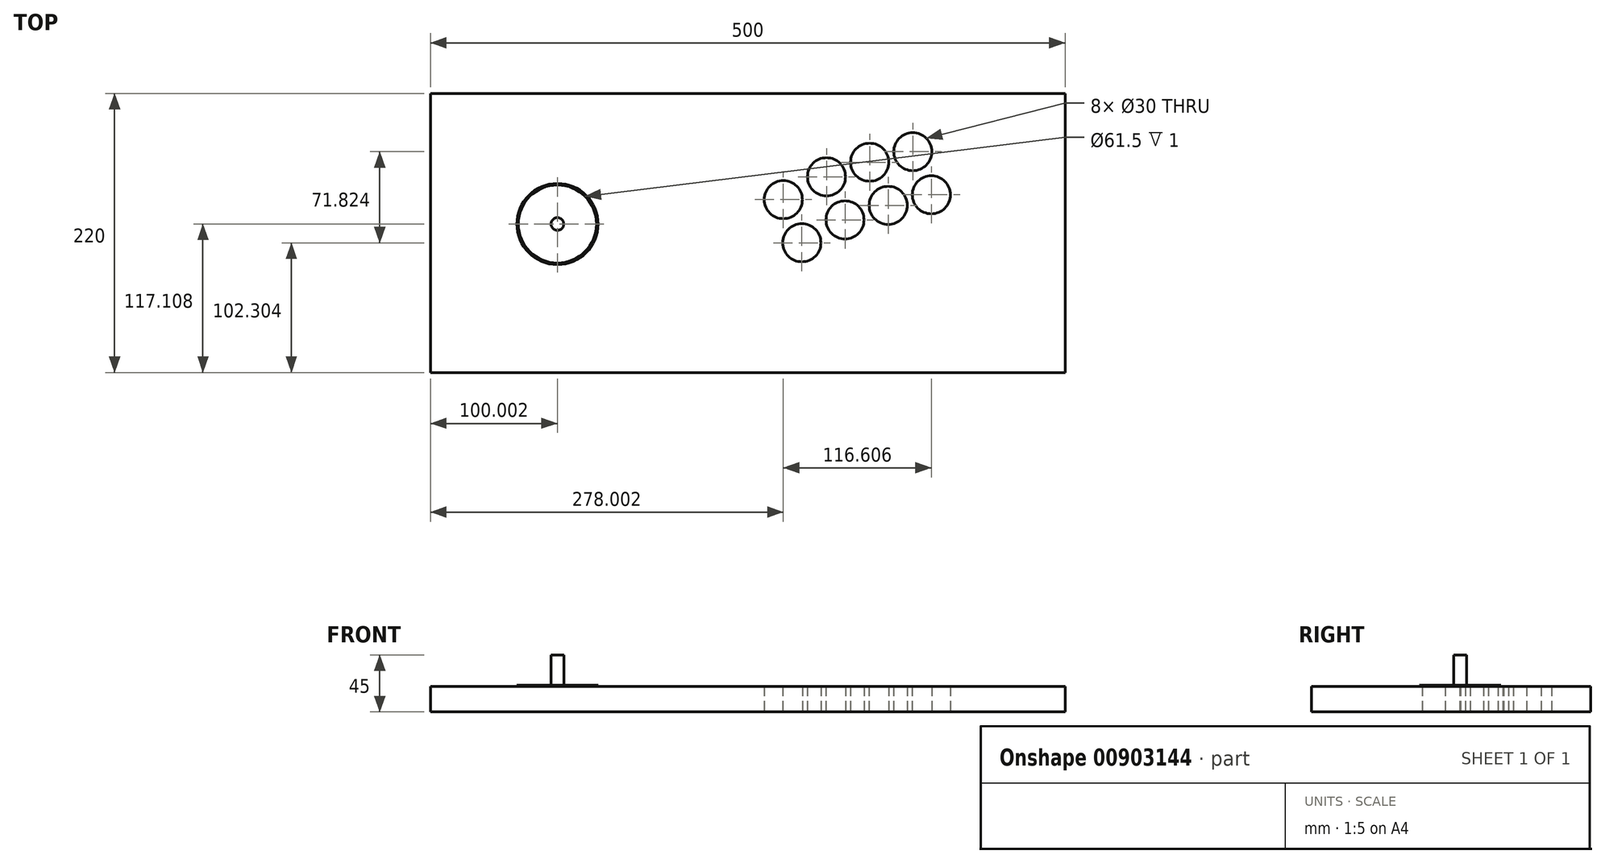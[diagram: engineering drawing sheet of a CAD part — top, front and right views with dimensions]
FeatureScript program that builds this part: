
annotation { "Feature Type Name" : "Feature", "Feature Type Description" : "" }
export const myFeature = defineFeature(function(context is Context, id is Id, definition is map)
    precondition{}
    {
        {
            var Q0;
            Q0=qCreatedBy(makeId("Top.planeOp"),FACE);
            var sketch = newSketch(context, id + "F0", { "sketchPlane" : qUnion([Q0])});
            skLineSegment(sketch, "E0.bottom", {"start": v(-215.53, 88.2) * mm, "end": v(284.47, 88.2) * mm});
            skLineSegment(sketch, "E0.left", {"start": v(-215.53, 88.2) * mm, "end": v(-215.53, -112.57) * mm});
            skLineSegment(sketch, "E0.right", {"start": v(284.47, 88.2) * mm, "end": v(284.47, -112.57) * mm});
            skLineSegment(sketch, "E1", {"start": v(-215.53, 88.2) * mm, "end": v(-215.53, -14.7) * mm});
            skLineSegment(sketch, "E2", {"start": v(-215.53, -14.7) * mm, "end": v(-115.53, -14.7) * mm, "construction": true});
            skCircle(sketch, "E3", {"center": v(-115.53, -14.7) * mm, "radius": 32 * mm});
            skCircle(sketch, "E4", {"center": v(62.47, 4.5) * mm, "radius": 15 * mm});
            skCircle(sketch, "E5", {"center": v(96.47, 22.55) * mm, "radius": 15 * mm});
            skCircle(sketch, "E6", {"center": v(77.08, -29.5) * mm, "radius": 15 * mm});
            skCircle(sketch, "E7", {"center": v(111.08, -11.45) * mm, "radius": 15 * mm});
            skCircle(sketch, "E8", {"center": v(145.08, 0) * mm, "radius": 15 * mm});
            skCircle(sketch, "E9", {"center": v(130.47, 34) * mm, "radius": 15 * mm});
            skCircle(sketch, "E10", {"center": v(179.08, 8.33) * mm, "radius": 15 * mm});
            skCircle(sketch, "E11", {"center": v(164.47, 42.33) * mm, "radius": 15 * mm});
            skCircle(sketch, "E12", {"center": v(-115.53, -14.7) * mm, "radius": 30.75 * mm});
            skCircle(sketch, "E13", {"center": v(-115.53, -14.7) * mm, "radius": 5 * mm});
            skLineSegment(sketch, "E14", {"start": v(-215.53, 88.2) * mm, "end": v(-215.53, -131.8) * mm});
            skLineSegment(sketch, "E15", {"start": v(-215.53, -131.8) * mm, "end": v(284.47, -131.8) * mm});
            skLineSegment(sketch, "E16", {"start": v(284.47, -131.8) * mm, "end": v(284.47, -112.57) * mm});
            skSolve(sketch);
        }
        {
            var Q0;
            {var subQ0=sQuery(id+"F0.wireOp",EDGE,"E0.bottom");Q0=makeQuery(id+"F0.imprint","IMPRINT",FACE,{"disambiguationData":[TD([[makeQuery(id+"F0.imprint","IMPRINT",EDGE,{"derivedFrom":subQ0}),-1.0]])]});}
            var Q1;
            Q1=makeQuery(id+"F0.imprint","IMPRINT",FACE,{"disambiguationData":[TD([[makeQuery(id+"F0.imprint","IMPRINT",EDGE,{"derivedFrom":sQuery(id+"F0.wireOp",EDGE,"E12")}),1.0]])]});
            var Q2;
            Q2=makeQuery(id+"F0.imprint","IMPRINT",FACE,{"disambiguationData":[TD([[makeQuery(id+"F0.imprint","IMPRINT",EDGE,{"derivedFrom":sQuery(id+"F0.wireOp",EDGE,"E13")}),1.0]])]});
            var Q3;
            Q3=makeQuery(id+"F0.imprint","IMPRINT",FACE,{"disambiguationData":[TD([[makeQuery(id+"F0.imprint","IMPRINT",EDGE,{"derivedFrom":sQuery(id+"F0.wireOp",EDGE,"E3")}),1.0]])]});
            extrude(context, id + "F1", {"entities" : qUnion([Q0, Q1, Q2, Q3]), "depth" : 20 * mm, "offsetDistance" : 25 * mm});
        }
        {
            var Q0;
            Q0=makeQuery(id+"F0.imprint","IMPRINT",FACE,{"disambiguationData":[TD([[makeQuery(id+"F0.imprint","IMPRINT",EDGE,{"derivedFrom":sQuery(id+"F0.wireOp",EDGE,"E3")}),1.0]])]});
            var Q1;
            Q1=sQuery(id+"F0.wireOp",EDGE,"E12");
            var Q2;
            Q2=sQuery(id+"F0.wireOp",EDGE,"E3");
            extrude(context, id + "F2", {"entities" : qUnion([Q0]), "operationType" : NewBodyOperationType.ADD, "surfaceEntities" : qUnion([Q1, Q2]), "depth" : 21 * mm, "offsetDistance" : 25 * mm});
        }
        {
            var Q0;
            Q0=makeQuery(id+"F0.imprint","IMPRINT",FACE,{"disambiguationData":[TD([[makeQuery(id+"F0.imprint","IMPRINT",EDGE,{"derivedFrom":sQuery(id+"F0.wireOp",EDGE,"E13")}),1.0]])]});
            extrude(context, id + "F3", {"entities" : qUnion([Q0]), "operationType" : NewBodyOperationType.ADD, "depth" : 45 * mm, "offsetDistance" : 25 * mm});
        }
    });
